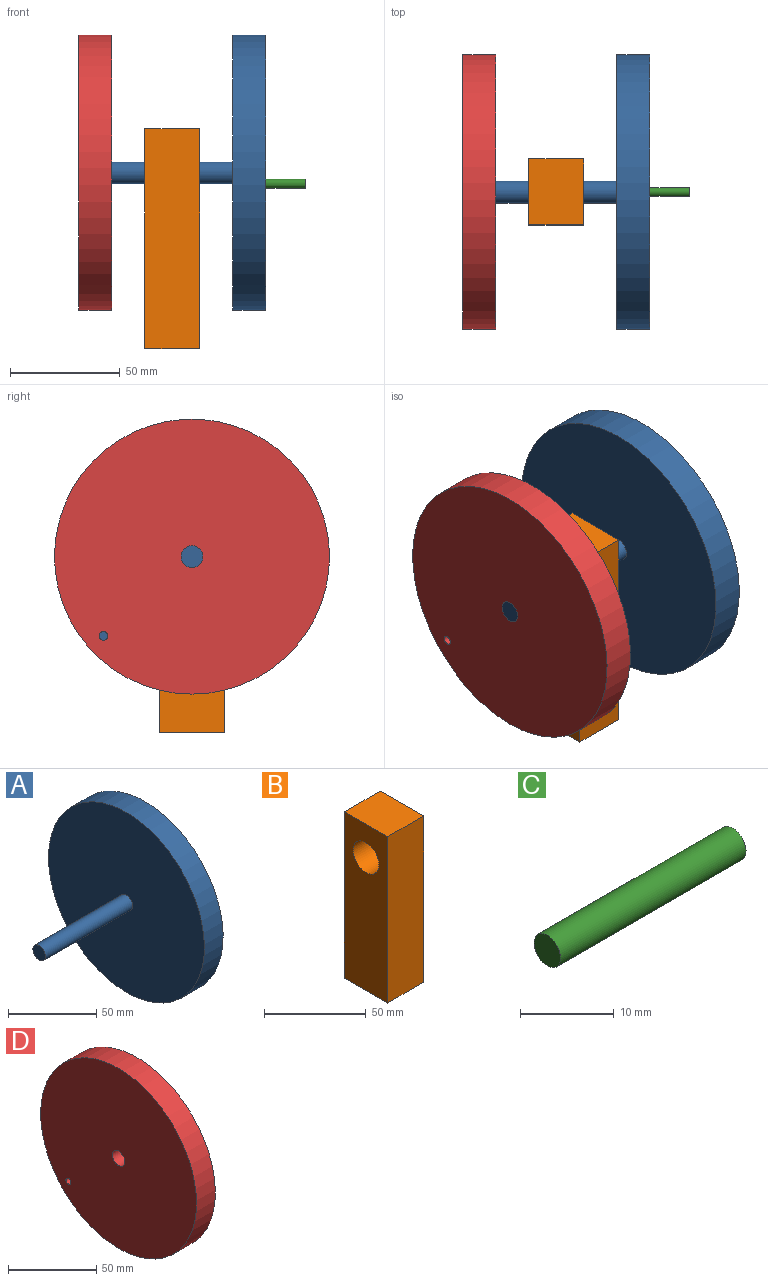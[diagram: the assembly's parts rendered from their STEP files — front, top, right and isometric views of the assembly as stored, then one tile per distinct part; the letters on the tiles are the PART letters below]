
ASSEMBLY  parts=4 mates=3
PART A: 7 faces, bbox 85x125x125 mm
  f0: cylinder r=1.5mm len=10mm, axis (-1,0,0), area 94.2mm2, adj f2,f6
  f1: cylinder r=62.5mm len=125mm, axis (-1,0,0), area 5890.5mm2, adj f2,f3
  f2: plane 125x125mm, normal (1,0,0), area 12264.8mm2, adj f0,f1
  f3: plane 125x125mm, normal (-1,0,0), area 12193.3mm2, adj f1,f4
  f4: cylinder r=5mm len=70mm, axis (1,0,0), area 2199.1mm2, adj f3,f5
  f5: plane 10x10mm, normal (-1,0,0), area 78.5mm2, adj f4
  f6: plane 3x3mm, normal (1,0,0), area 7.1mm2, adj f0
PART B: 7 faces, bbox 25x30x100 mm
  f0: plane 100x25mm, normal (0,-1,0), area 2500mm2, adj f1,f4,f5,f6
  f1: plane 30x25mm, normal (0,0,-1), area 750mm2, adj f0,f2,f5,f6
  f2: plane 100x25mm, normal (0,1,0), area 2500mm2, adj f1,f4,f5,f6
  f3: cylinder r=9mm len=25mm, axis (-1,0,0), area 1413.7mm2, adj f5,f6
  f4: plane 30x25mm, normal (0,0,1), area 750mm2, adj f0,f2,f5,f6
  f5: plane 100x30mm, normal (1,0,0), area 2745.5mm2, adj f0,f1,f2,f3,f4
  f6: plane 100x30mm, normal (-1,0,0), area 2745.5mm2, adj f0,f1,f2,f3,f4
PART C: 3 faces, bbox 28x4x4 mm
  f0: cylinder r=2mm len=28mm, axis (-1,0,0), area 351.9mm2, adj f1,f2
  f1: plane 4x4mm, normal (1,0,0), area 12.6mm2, adj f0
  f2: plane 4x4mm, normal (-1,0,0), area 12.6mm2, adj f0
PART D: 5 faces, bbox 15x125x125 mm
  f0: cylinder r=5mm len=15mm, axis (-1,0,0), area 471.2mm2, adj f3,f4
  f1: cylinder r=2mm len=15mm, axis (-1,0,0), area 188.5mm2, adj f3,f4
  f2: cylinder r=62.5mm len=125mm, axis (-1,0,0), area 5890.5mm2, adj f3,f4
  f3: plane 125x125mm, normal (1,0,0), area 12180.7mm2, adj f0,f1,f2
  f4: plane 125x125mm, normal (-1,0,0), area 12180.7mm2, adj f0,f1,f2
PLACE A rot(axis=(1,0,0),0deg) t=(100.24,-29.98,96.48)mm
PLACE B t=(60.24,-29.98,16.48)mm fixed
PLACE C rot(axis=(1,0,0),0deg) t=(105.24,-29.98,91.48)mm
PLACE D t=(30.24,-29.98,96.48)mm
MATE revolute A.f4 <-> D.f2  axis (-1,0,0) through (30.24,-29.98,96.48)mm
MATE fastened C.f0 <-> A.f0  axis (-1,0,0) through (105.24,-29.98,91.48)mm
MATE revolute D.f0 <-> B.f3  axis (-1,0,0) through (30.24,-29.98,96.48)mm
